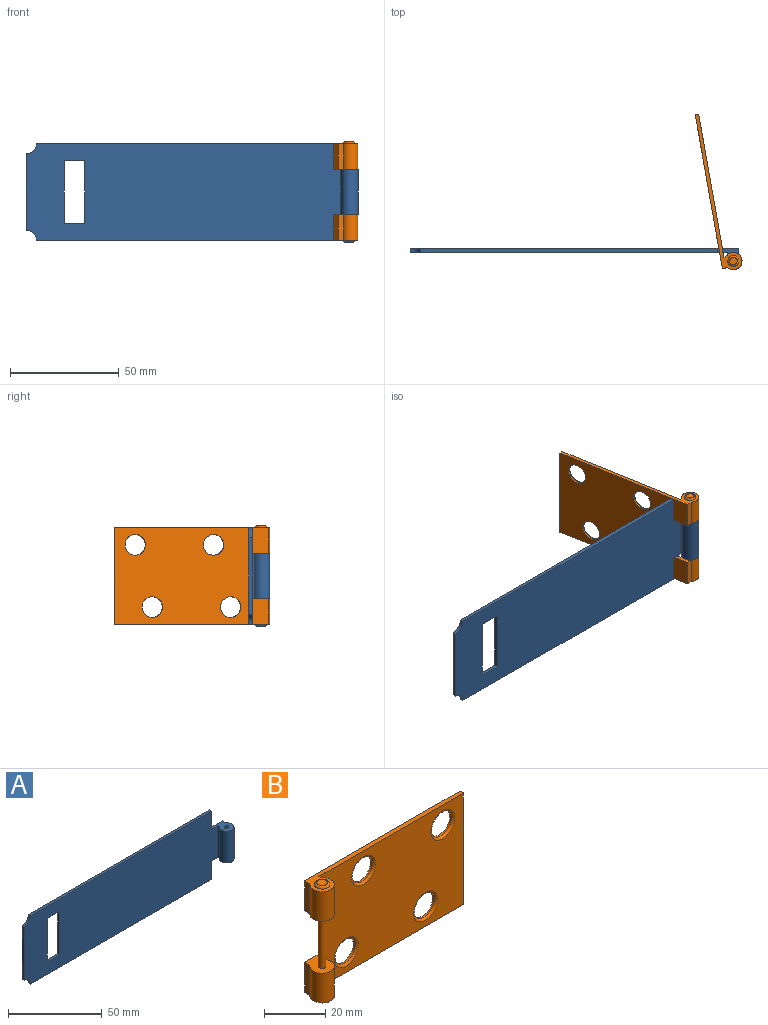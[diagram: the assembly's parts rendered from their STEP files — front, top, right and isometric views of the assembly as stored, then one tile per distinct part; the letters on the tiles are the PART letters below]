
ASSEMBLY  parts=2 mates=1
PART A: 19 faces, bbox 152.4x9.5x44.5 mm
  f0: plane 9.53x1.59mm, normal (0,0,1), area 15.1mm2, adj f1,f12,f13,f14
  f1: plane 28.58x1.59mm, normal (1,0,0), area 45.4mm2, adj f0,f2,f13,f14
  f2: plane 9.53x1.59mm, normal (0,0,-1), area 15.1mm2, adj f1,f12,f13,f14
  f3: plane 136.53x1.59mm, normal (0,0,1), area 216.7mm2, adj f4,f11,f13,f14
  f4: cylinder r=4.76mm len=4.76mm, axis (0,1,0), area 11.9mm2, adj f3,f5,f13,f14
  f5: plane 34.93x1.59mm, normal (-1,0,0), area 55.4mm2, adj f4,f6,f13,f14
  f6: cylinder r=4.76mm len=4.76mm, axis (0,1,0), area 11.9mm2, adj f5,f7,f13,f14
  f7: plane 136.53x1.59mm, normal (0,0,-1), area 216.7mm2, adj f6,f8,f13,f14
  f8: plane 11.91x1.59mm, normal (1,0,0), area 18.9mm2, adj f7,f9,f13,f14
  f9: plane 11.11x9.53mm, normal (0,0,-1), area 61.3mm2, adj f8,f13,f14,f15,f16,f17,f18
  f10: plane 11.11x9.53mm, normal (0,0,1), area 61.3mm2, adj f11,f13,f14,f15,f16,f17,f18
  f11: plane 11.91x1.59mm, normal (1,0,0), area 18.9mm2, adj f3,f10,f13,f14
  f12: plane 28.58x1.59mm, normal (-1,0,0), area 45.4mm2, adj f0,f2,f13,f14
  f13: plane 145.89x44.45mm, normal (0,-1,0), area 6067.4mm2, adj f0,f1,f2,f3,f4,f5,f6,f7
  f14: plane 150.97x44.45mm, normal (0,1,0), area 6172.3mm2, adj f0,f1,f2,f3,f4,f5,f6,f7
  f15: cylinder r=1.27mm len=20.64mm, axis (0,0,1), area 164.7mm2, adj f9,f10
  f16: cylinder r=3.97mm len=20.64mm, axis (0,0,1), area 400.9mm2, adj f9,f10,f17,f18
  f17: plane 20.64x0.92mm, normal (-1,0,0), area 19mm2, adj f9,f10,f13,f16
  f18: plane 20.64x2.51mm, normal (1,0,0), area 51.7mm2, adj f9,f10,f14,f16
PART B: 27 faces, bbox 73.1x9.5x46.1 mm
  f0: plane 66.6x44.45mm, normal (0,-1,0), area 2508.3mm2, adj f1,f2,f4,f5,f6,f8,f11,f12
  f1: plane 20.64x1.59mm, normal (-1,0,0), area 32.8mm2, adj f0,f2,f8,f9
  f2: plane 9.62x9.54mm, normal (0,0,-1), area 58.8mm2, adj f0,f1,f3,f9,f12,f13,f15
  f3: plane 11.91x2.51mm, normal (-1,0,0), area 29.8mm2, adj f2,f4,f9,f13
  f4: plane 73.1x9.53mm, normal (0,0,1), area 144.5mm2, adj f0,f3,f5,f9,f12,f13,f18
  f5: plane 44.45x1.59mm, normal (1,0,0), area 70.6mm2, adj f0,f4,f6,f9
  f6: plane 73.1x9.53mm, normal (0,0,-1), area 144.5mm2, adj f0,f5,f7,f9,f10,f11,f17
  f7: plane 11.91x2.51mm, normal (-1,0,0), area 29.8mm2, adj f6,f8,f9,f10
  f8: plane 9.62x9.54mm, normal (0,0,1), area 58.9mm2, adj f0,f1,f7,f9,f10,f11,f15
  f9: plane 71.68x44.45mm, normal (0,1,0), area 2732.2mm2, adj f1,f2,f3,f4,f5,f6,f7,f8
  f10: cylinder r=3.97mm len=11.91mm, axis (0,0,1), area 231.3mm2, adj f6,f7,f8,f11
  f11: plane 11.91x0.92mm, normal (1,0,0), area 10.9mm2, adj f0,f6,f8,f10
  f12: plane 11.91x0.92mm, normal (1,0,0), area 10.9mm2, adj f0,f2,f4,f13
  f13: cylinder r=3.97mm len=11.91mm, axis (0,0,-1), area 231.3mm2, adj f2,f3,f4,f12
  f14: plane 3.49x3.49mm, normal (0,0,1), area 9.6mm2, adj f18
  f15: cylinder r=1.27mm len=20.64mm, axis (0,0,1), area 164.1mm2, adj f2,f8
  f16: plane 3.49x3.49mm, normal (0,0,-1), area 9.6mm2, adj f17
  f17: torus R=1.75mm, axis (0,0,-1), area 17.6mm2, adj f6,f16
  f18: torus R=1.75mm, axis (0,0,1), area 17.6mm2, adj f4,f14
  f19: cylinder r=4.76mm len=9.53mm, axis (0,-1,0), area 23.8mm2, adj f9,f26
  f20: cylinder r=4.76mm len=9.53mm, axis (0,-1,0), area 23.8mm2, adj f9,f25
  f21: cylinder r=4.76mm len=9.53mm, axis (0,-1,0), area 23.8mm2, adj f9,f24
  f22: cylinder r=4.76mm len=9.53mm, axis (0,-1,0), area 23.8mm2, adj f9,f23
  f23: torus R=5.56mm, axis (0,1,0), area 39.6mm2, adj f0,f22
  f24: torus R=5.56mm, axis (0,1,0), area 39.6mm2, adj f0,f21
  f25: torus R=5.56mm, axis (0,1,0), area 39.6mm2, adj f0,f20
  f26: torus R=5.56mm, axis (0,1,0), area 39.6mm2, adj f0,f19
PLACE A at identity fixed
PLACE B rot(axis=(0,0,1),100deg) t=(168.73,-152.7,0)mm
MATE revolute B.f10 <-> A.f15  axis (0,0,1) through (148.43,-5.56,11.91)mm
